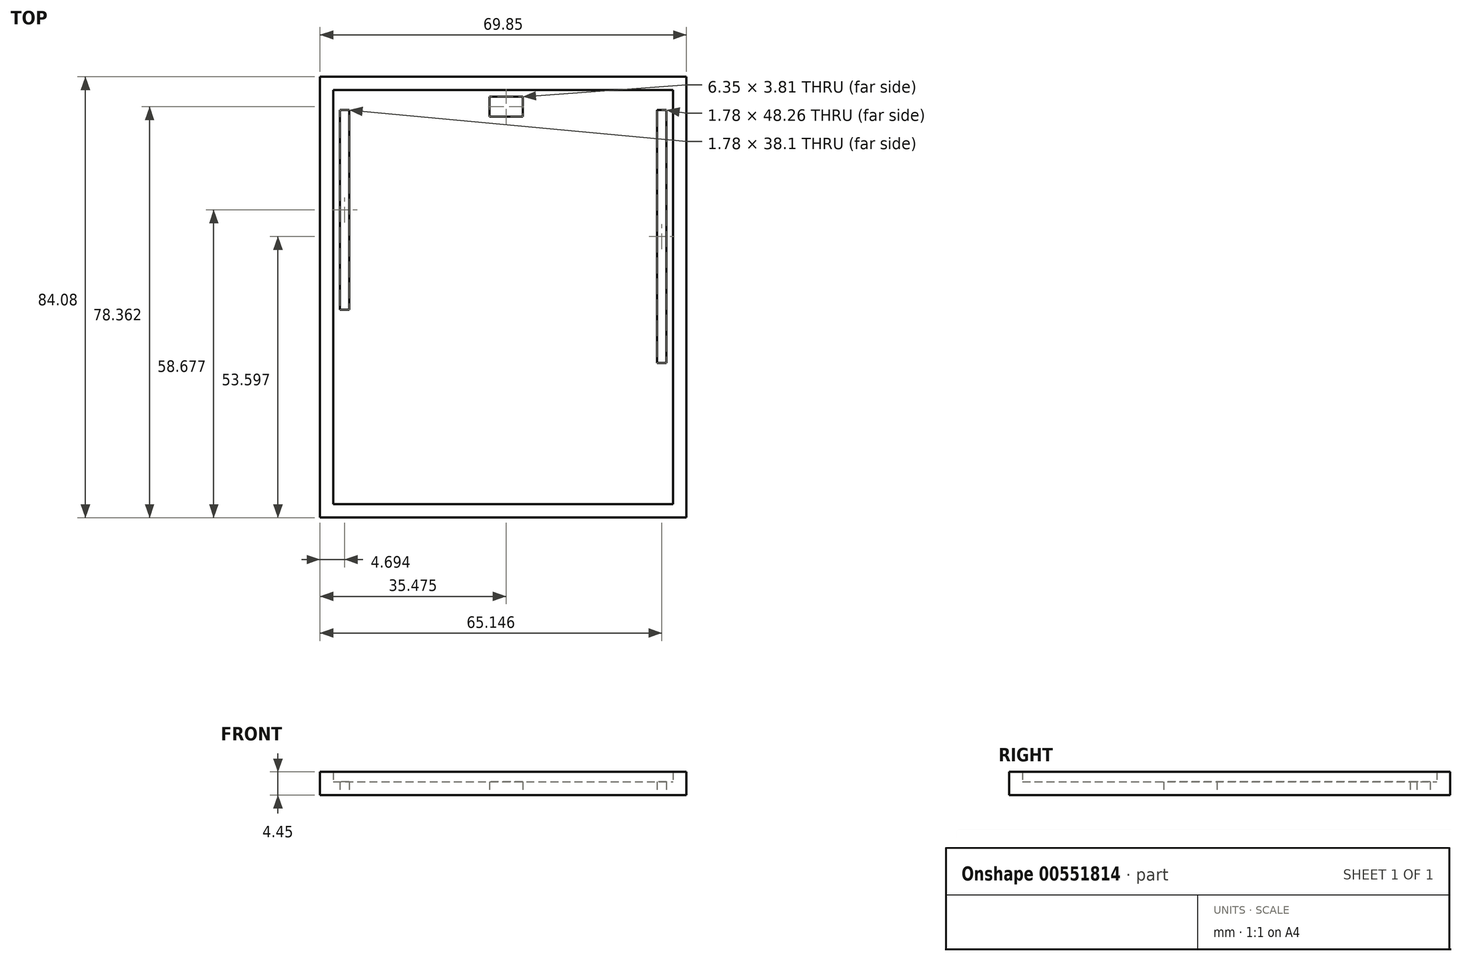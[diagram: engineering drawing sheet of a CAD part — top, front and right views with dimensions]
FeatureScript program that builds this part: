
annotation { "Feature Type Name" : "Feature", "Feature Type Description" : "" }
export const myFeature = defineFeature(function(context is Context, id is Id, definition is map)
    precondition{}
    {
        {
            var Q0;
            Q0=qCreatedBy(makeId("Front.planeOp"),FACE);
            var sketch = newSketch(context, id + "F0", { "sketchPlane" : qUnion([Q0])});
            skLineSegment(sketch, "E0.bottom", {"start": v(-32.3, -11.88) * mm, "end": v(37.55, -11.88) * mm});
            skLineSegment(sketch, "E0.top", {"start": v(-32.3, -16.33) * mm, "end": v(37.55, -16.33) * mm});
            skLineSegment(sketch, "E0.left", {"start": v(-32.3, -11.88) * mm, "end": v(-32.3, -16.33) * mm});
            skLineSegment(sketch, "E0.right", {"start": v(37.55, -11.88) * mm, "end": v(37.55, -16.33) * mm});
            skSolve(sketch);
        }
        {
            var Q0;
            Q0=makeQuery(id+"F0.imprint","IMPRINT",FACE,{"disambiguationData":[TD([[makeQuery(id+"F0.imprint","IMPRINT",EDGE,{"derivedFrom":sQuery(id+"F0.wireOp",EDGE,"E0.bottom")}),-1.0]])]});
            extrude(context, id + "F1", {"entities" : qUnion([Q0]), "endBound" : BoundingType.SYMMETRIC, "depth" : 84.07 * mm, "offsetDistance" : 25.4 * mm});
        }
        {
            var Q0;
            Q0=makeQuery(id+"F1.opExtrude","SWEPT_FACE",FACE,{"disambiguationData":[OSD([sQuery(id+"F0.wireOp",EDGE,"E0.bottom")])]});
            shell(context, id + "F2", {"entities" : qUnion([Q0]), "thickness" : 2.54 * mm});
        }
        {
            var Q0;
            Q0=makeQuery(id+"F1.opExtrude","SWEPT_FACE",FACE,{"disambiguationData":[OSD([sQuery(id+"F0.wireOp",EDGE,"E0.top")])]});
            var sketch = newSketch(context, id + "F3", { "sketchPlane" : qUnion([Q0])});
            skLineSegment(sketch, "E1.bottom", {"start": v(31.96, 12.57) * mm, "end": v(33.74, 12.57) * mm});
            skLineSegment(sketch, "E1.top", {"start": v(31.96, -35.69) * mm, "end": v(33.74, -35.69) * mm});
            skLineSegment(sketch, "E1.left", {"start": v(31.96, 12.57) * mm, "end": v(31.96, -35.69) * mm});
            skLineSegment(sketch, "E1.right", {"start": v(33.74, 12.57) * mm, "end": v(33.74, -35.69) * mm});
            skLineSegment(sketch, "E2.bottom", {"start": v(0, -34.42) * mm, "end": v(6.35, -34.42) * mm});
            skLineSegment(sketch, "E2.top", {"start": v(0, -38.23) * mm, "end": v(6.35, -38.23) * mm});
            skLineSegment(sketch, "E2.left", {"start": v(0, -34.42) * mm, "end": v(0, -38.23) * mm});
            skLineSegment(sketch, "E2.right", {"start": v(6.35, -34.42) * mm, "end": v(6.35, -38.23) * mm});
            skLineSegment(sketch, "E3.bottom", {"start": v(-28.5, 2.41) * mm, "end": v(-26.72, 2.41) * mm});
            skLineSegment(sketch, "E3.top", {"start": v(-28.5, -35.69) * mm, "end": v(-26.72, -35.69) * mm});
            skLineSegment(sketch, "E3.left", {"start": v(-28.5, 2.41) * mm, "end": v(-28.5, -35.69) * mm});
            skLineSegment(sketch, "E3.right", {"start": v(-26.72, 2.41) * mm, "end": v(-26.72, -35.69) * mm});
            skSolve(sketch);
        }
        {
            var Q0;
            Q0=makeQuery(id+"F3.imprint","IMPRINT",FACE,{"disambiguationData":[TD([[makeQuery(id+"F3.imprint","IMPRINT",EDGE,{"derivedFrom":sQuery(id+"F3.wireOp",EDGE,"E3.bottom")}),-1.0]])]});
            var Q1;
            Q1=makeQuery(id+"F3.imprint","IMPRINT",FACE,{"disambiguationData":[TD([[makeQuery(id+"F3.imprint","IMPRINT",EDGE,{"derivedFrom":sQuery(id+"F3.wireOp",EDGE,"E2.bottom")}),-1.0]])]});
            var Q2;
            Q2=makeQuery(id+"F3.imprint","IMPRINT",FACE,{"disambiguationData":[TD([[makeQuery(id+"F3.imprint","IMPRINT",EDGE,{"derivedFrom":sQuery(id+"F3.wireOp",EDGE,"E1.bottom")}),-1.0]])]});
            extrude(context, id + "F4", {"entities" : qUnion([Q0, Q1, Q2]), "operationType" : NewBodyOperationType.REMOVE, "oppositeDirection" : true, "depth" : 25.4 * mm, "offsetDistance" : 25.4 * mm});
        }
    });
